# Revit family: Gripple Twist Clamp
name_source: partatom
category: Specialty Equipment
revit_build: Autodesk Revit 2017 (Build: 20160225_1515(x64)
units: mm (PartAtom-declared; Revit-internal decimal feet)

## family parameters
Always vertical = No
Cut with Voids When Loaded = No
OmniClass Number = 23.45.00.00
OmniClass Title = Sanitary, Laundry, and Cleaning Equipment
Part Type = Normal
Room Calculation Point = No
Round Connector Dimension = Use Diameter
Shared = Yes
Work Plane-Based = Yes

## types (2) — shared parameters
-width/2 = -15 mm  [stored -0.0492126 ft]
A = 7 mm  [stored 0.0229659 ft]
B = 10 mm  [stored 0.0328084 ft]
C = 4 mm  [stored 0.0131234 ft]
CAF = 13 mm  [stored 0.0426509 ft]
CD = 20 mm  [stored 0.0656168 ft]
HL = 20 mm  [stored 0.0656168 ft]
HW = 10 mm  [stored 0.0328084 ft]
Manufacturer = Gripple Ltd
T = 2 mm  [stored 0.00656168 ft]
URL = http://www.gripple.co.uk
W = 30 mm  [stored 0.0984252 ft]
W/2 = 15 mm  [stored 0.0492126 ft]
WD = 2 mm  [stored 0.00656168 ft]
zero-valued in all types: Cost, Default Elevation

## per-type parameters (varying)
| type | H | Model |
| QT-T | 35 mm  [stored 0.114829 ft] | Quarter Turn Clamp - Standard |
| QT-C | 1 mm  [stored 0.00328084 ft] | Quarter Turn Clamp - Compact |

note: column(s) folded — value = type name in every type: Assembly Code

note: [stored X ft] marks values corroborated as IEEE doubles in the binary element streams (Revit-internal decimal feet)

## geometry (parser evidence)
native form markers: Blend x2, Sweep x3
no freeform markers — native parametric forms only
